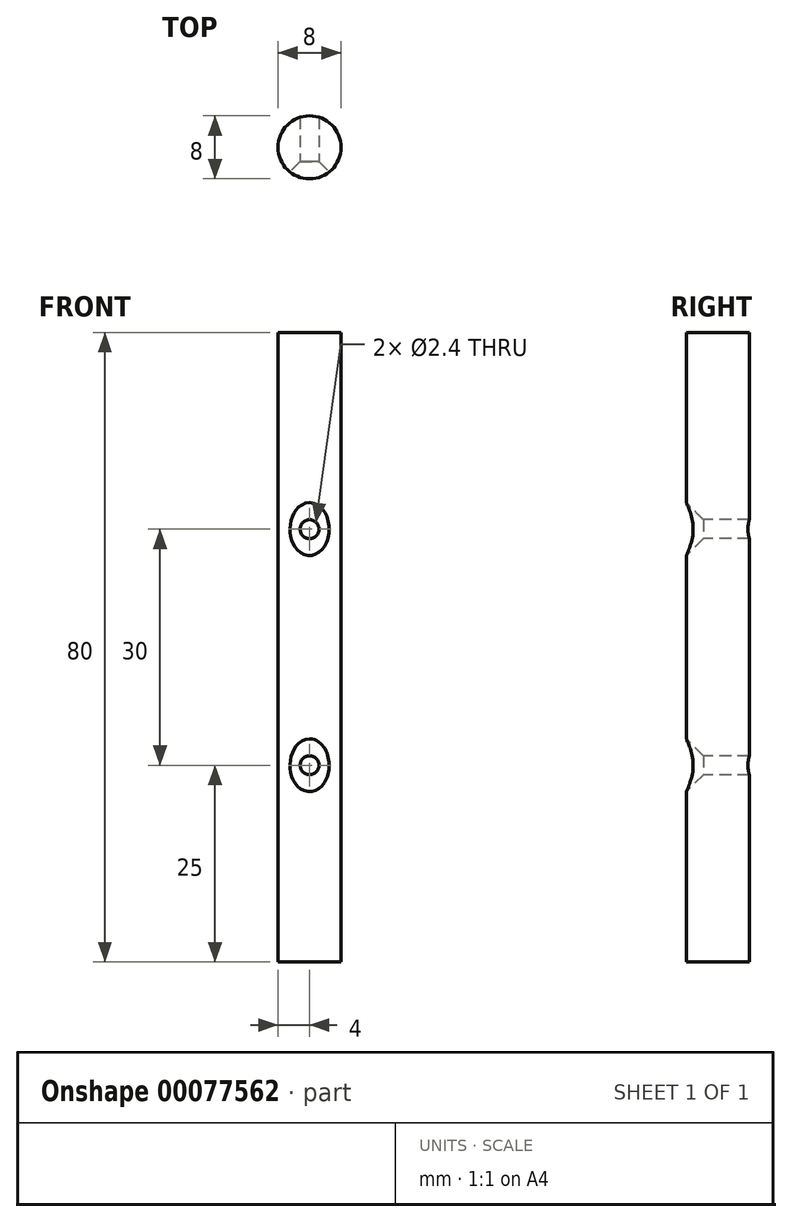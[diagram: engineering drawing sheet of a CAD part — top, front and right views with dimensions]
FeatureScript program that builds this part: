
annotation { "Feature Type Name" : "Feature", "Feature Type Description" : "" }
export const myFeature = defineFeature(function(context is Context, id is Id, definition is map)
    precondition{}
    {
        {
            var Q0;
            Q0=qCreatedBy(makeId("Top.planeOp"),FACE);
            var sketch = newSketch(context, id + "F0", { "sketchPlane" : qUnion([Q0])});
            skCircle(sketch, "E0", {"center": v(0, 0) * mm, "radius": 4 * mm});
            skSolve(sketch);
        }
        {
            var Q0;
            Q0=makeQuery(id+"F0.imprint","IMPRINT",FACE,{"disambiguationData":[TD([[makeQuery(id+"F0.imprint","IMPRINT",EDGE,{"derivedFrom":sQuery(id+"F0.wireOp",EDGE,"E0")}),1.0]])]});
            var Q1;
            Q1=sQuery(id+"F0.wireOp",EDGE,"E0");
            extrude(context, id + "F1", {"entities" : qUnion([Q0]), "surfaceEntities" : qUnion([Q1]), "depth" : 80 * mm});
        }
        {
            var Q0;
            Q0=qCreatedBy(makeId("Front.planeOp"),FACE);
            cPlane(context, id + "F2", {"entities" : qUnion([Q0]), "cplaneType" : CPlaneType.OFFSET, "offset" : 4 * mm, "oppositeDirection" : true, "width" : 150 * mm, "height" : 150 * mm});
        }
        {
            var Q0;
            Q0=qCreatedBy(id+"F2.planeOp",FACE);
            var sketch = newSketch(context, id + "F3", { "sketchPlane" : qUnion([Q0])});
            skPoint(sketch, "E1", {"position": v(0, 25) * mm});
            skPoint(sketch, "E2.0.1.0", {"position": v(0, 55) * mm});
            skLineSegment(sketch, "E2.direction1", {"start": v(0, 25) * mm, "end": v(25, 25) * mm, "construction": true});
            skLineSegment(sketch, "E2.direction2", {"start": v(0, 25) * mm, "end": v(0, 55) * mm, "construction": true});
            skSolve(sketch);
        }
        {
            var Q0;
            Q0=sQuery(id+"F3.wireOp",VERTEX,"E2.0.1.0");
            var Q1;
            Q1=sQuery(id+"F3.wireOp",VERTEX,"E1");
            var Q2;
            Q2=makeQuery(id+"F1.opExtrude","SWEPT_BODY",BODY,{"disambiguationData":[OSD([sQuery(id+"F0.wireOp",EDGE,"E0")])]});
            hole(context, id + "F4", {"style" : HoleStyle.C_SINK, "endStyle" : HoleEndStyle.BLIND, "oppositeDirection" : true, "standardTappedOrClearance" : lookupTablePath({ "standard" : "ISO", "engagement" : "75%", "pitch" : "0.6 mm", "size" : "M3", "type" : "Tapped" }), "standardBlindInLast" : lookupTablePath({ "standard" : "ISO", "engagement" : "75%", "pitch" : "0.6 mm", "size" : "M3", "type" : "Tapped" }), "holeDiameter" : 2.4 * mm, "cSinkDiameter" : 6.72 * mm, "cSinkAngle" : 90 * degree, "holeDepth" : 50 * mm, "startFromSketch" : true, "locations" : qUnion([Q0, Q1]), "scope" : qUnion([Q2])});
        }
        {
            var Q0;
            Q0=makeQuery(id+"F1.opExtrude","SWEPT_BODY",BODY,{"disambiguationData":[OSD([sQuery(id+"F0.wireOp",EDGE,"E0")])]});
            var Q1;
            Q1=makeQuery(id+"F1.opExtrude","CAP_EDGE",EDGE,{"disambiguationData":[OSD([sQuery(id+"F0.wireOp",EDGE,"E0")])],"isStart":false});
            transform(context, id + "F5", {"entities" : qUnion([Q0]), "transformType" : TransformType.ROTATION, "transformAxis" : qUnion([Q1]), "angle" : 180 * degree, "makeCopy" : false});
        }
    });
